# Revit family: Warp-9
name_source: partatom
category: Lighting Fixtures
units: mm (PartAtom-declared; Revit-internal decimal feet)

## family parameters
Always vertical = Yes
Cut with Voids When Loaded = No
Light Source = Yes
OmniClass Number = 23.80.70.14.21
OmniClass Title = Street and Roadway Lighting
Part Type = Normal
Room Calculation Point = No
Round Connector Dimension = Use Diameter
Shared = No
Work Plane-Based = No

## types (2) — shared parameters
Assembly Code = D5020230
Color Filter = 16777215
Default Elevation = 0' - 0"
Description = Large, Electronic LED
Dimming Lamp Color Temperature Shift = <None>
Emit Shape Visible in Rendering = No
Emit from Rectangle Length = 1' - 0"
Emit from Rectangle Width = 1' - 0"
Fixture Height = 0' - 7 1/16"
Glass = Glass
Lamp = LED
Light Case = Aluminum_Black-powder-coat
Load Classification = Lighting
Manufacturer = Kim Lighting
MasterFormat Title = Site Lighting
Model = Wrap 9
Note Visible = Yes
Number of Poles = 1
OmniClass Number = 23.80.70.14.21
OmniClass Title = Streets an Roadway Lighting
Photometric Notes = More IES files download on Photometric Web Link
Pole Finish = Aluminum-Black
Power Factor = 1
Series = Site/Roadway
URL = https://www.currentlighting.com
Voltage = 277 V
Wattage Comments = 131W to 270W

## per-type parameters (varying)
| type | Apparent Load | Fixture Length | Fixture Mount Height | Fixture Mount Length | Fixture Total  Height | Height | Photometric Web File | Tilt Angle | Watts | Weight | Width |
| WP9L | 175 VA | 2' - 11 1/8" | 0' - 5 27/32" | 0' - 5 1/8" | 0' - 10 5/16" | 0' - 5 1/2" | wp9l2p70-120l5k.ies | 90.00° | 175 W | 0.04 kip | 1' - 8" |
| WP9S | 88 VA | 2' - 2 15/16" | 0' - 5 9/16" | 0' - 4 7/16" | 0' - 8 15/16" | 0' - 4 1/8" | wp9s3p70-60l4k.ies | 60.00° | 88 W | 0.02 kip | 1' - 3" |

## geometry (parser evidence)
native form markers: Blend x2, Sweep x7
no freeform markers — native parametric forms only
